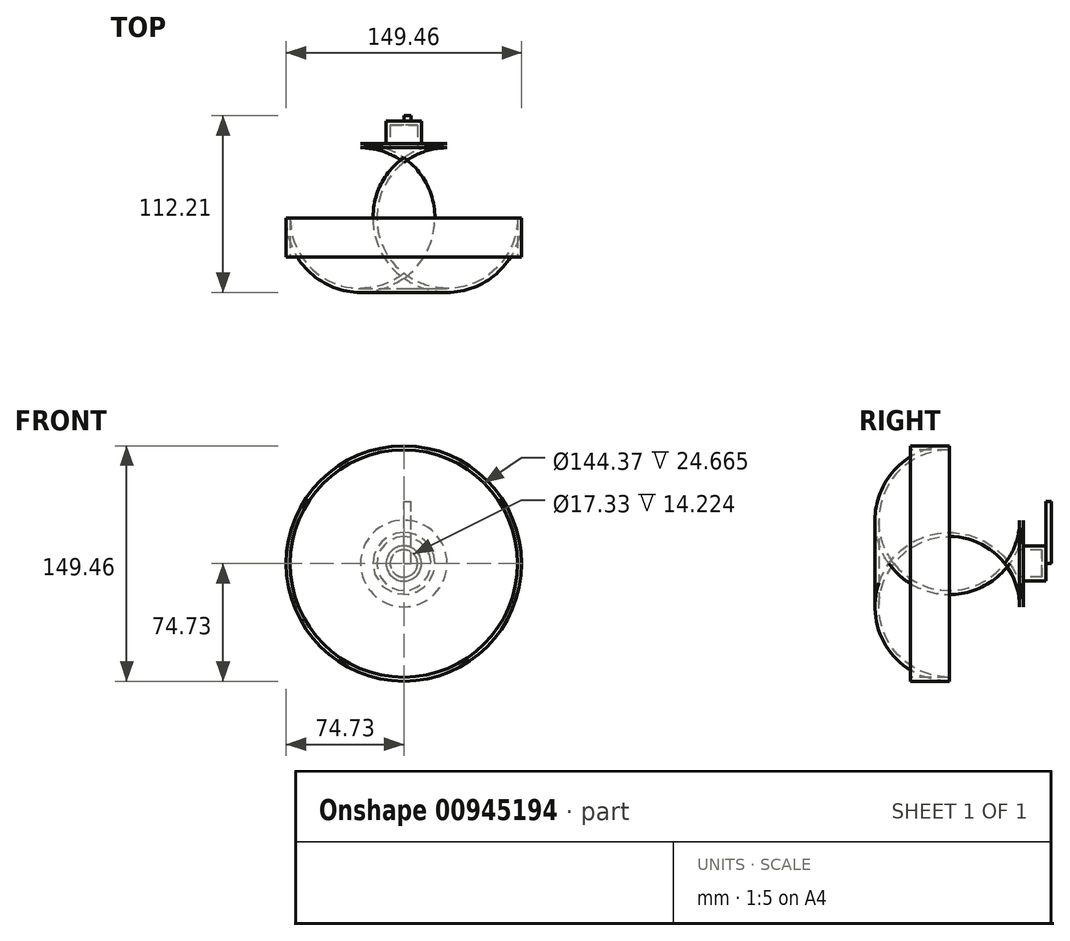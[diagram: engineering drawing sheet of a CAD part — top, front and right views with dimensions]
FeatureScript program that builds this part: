
annotation { "Feature Type Name" : "Feature", "Feature Type Description" : "" }
export const myFeature = defineFeature(function(context is Context, id is Id, definition is map)
    precondition{}
    {
        {
            var Q0;
            Q0=qCreatedBy(makeId("Front.planeOp"),FACE);
            var sketch = newSketch(context, id + "F0", { "sketchPlane" : qUnion([Q0])});
            skCircle(sketch, "E0", {"center": v(0, 0) * mm, "radius": 74.73 * mm});
            skSolve(sketch);
        }
        {
            var Q0;
            Q0 = qSketchRegion(id + "F0", true);
            extrude(context, id + "F1", {"entities" : qUnion([Q0]), "oppositeDirection" : true, "depth" : 71.88 * mm, "offsetDistance" : 25.4 * mm});
        }
        {
            var Q0;
            Q0=makeQuery(id+"F1.opExtrude","CAP_FACE",FACE,{"disambiguationData":[OSD([sQuery(id+"F0.wireOp",EDGE,"E0")])],"isStart":false});
            fillet(context, id + "F2", {"entities" : qUnion([Q0]), "radius" : 47.22 * mm, "tangentPropagation" : true, "allowEdgeOverflow" : false});
        }
        {
            var Q0;
            Q0=makeQuery(id+"F1.opExtrude","CAP_FACE",FACE,{"disambiguationData":[OSD([sQuery(id+"F0.wireOp",EDGE,"E0")])],"isStart":false});
            var sketch = newSketch(context, id + "F3", { "sketchPlane" : qUnion([Q0])});
            skCircle(sketch, "E1", {"center": v(0, 0) * mm, "radius": 11.2 * mm});
            skSolve(sketch);
        }
        {
            var Q0;
            Q0=makeQuery(id+"F3.imprint","IMPRINT",FACE,{"disambiguationData":[TD([[makeQuery(id+"F3.imprint","IMPRINT",EDGE,{"derivedFrom":sQuery(id+"F3.wireOp",EDGE,"E1")}),1.0]])]});
            extrude(context, id + "F4", {"entities" : qUnion([Q0]), "operationType" : NewBodyOperationType.ADD, "depth" : 14.22 * mm, "offsetDistance" : 25.4 * mm});
        }
        {
            var Q0;
            Q0=makeQuery(id+"F4.opExtrude","CAP_FACE",FACE,{"disambiguationData":[OSD([sQuery(id+"F3.wireOp",EDGE,"E1")])],"isStart":false});
            var sketch = newSketch(context, id + "F5", { "sketchPlane" : qUnion([Q0])});
            skLineSegment(sketch, "E2.bottom", {"start": v(0, 0) * mm, "end": v(-4.68, 0) * mm});
            skLineSegment(sketch, "E2.top", {"start": v(0, 39.34) * mm, "end": v(-4.68, 39.34) * mm});
            skLineSegment(sketch, "E2.left", {"start": v(0, 0) * mm, "end": v(0, 39.34) * mm});
            skLineSegment(sketch, "E2.right", {"start": v(-4.68, 0) * mm, "end": v(-4.68, 39.34) * mm});
            skSolve(sketch);
        }
        {
            var Q0;
            Q0 = qSketchRegion(id + "F5", true);
            extrude(context, id + "F6", {"entities" : qUnion([Q0]), "operationType" : NewBodyOperationType.ADD, "depth" : 3.56 * mm, "offsetDistance" : 25.4 * mm});
        }
        {
            var Q0;
            Q0=makeQuery(id+"F1.opExtrude","CAP_FACE",FACE,{"disambiguationData":[OSD([sQuery(id+"F0.wireOp",EDGE,"E0")])],"isStart":true});
            shell(context, id + "F7", {"entities" : qUnion([Q0]), "thickness" : 2.54 * mm});
        }
    });
